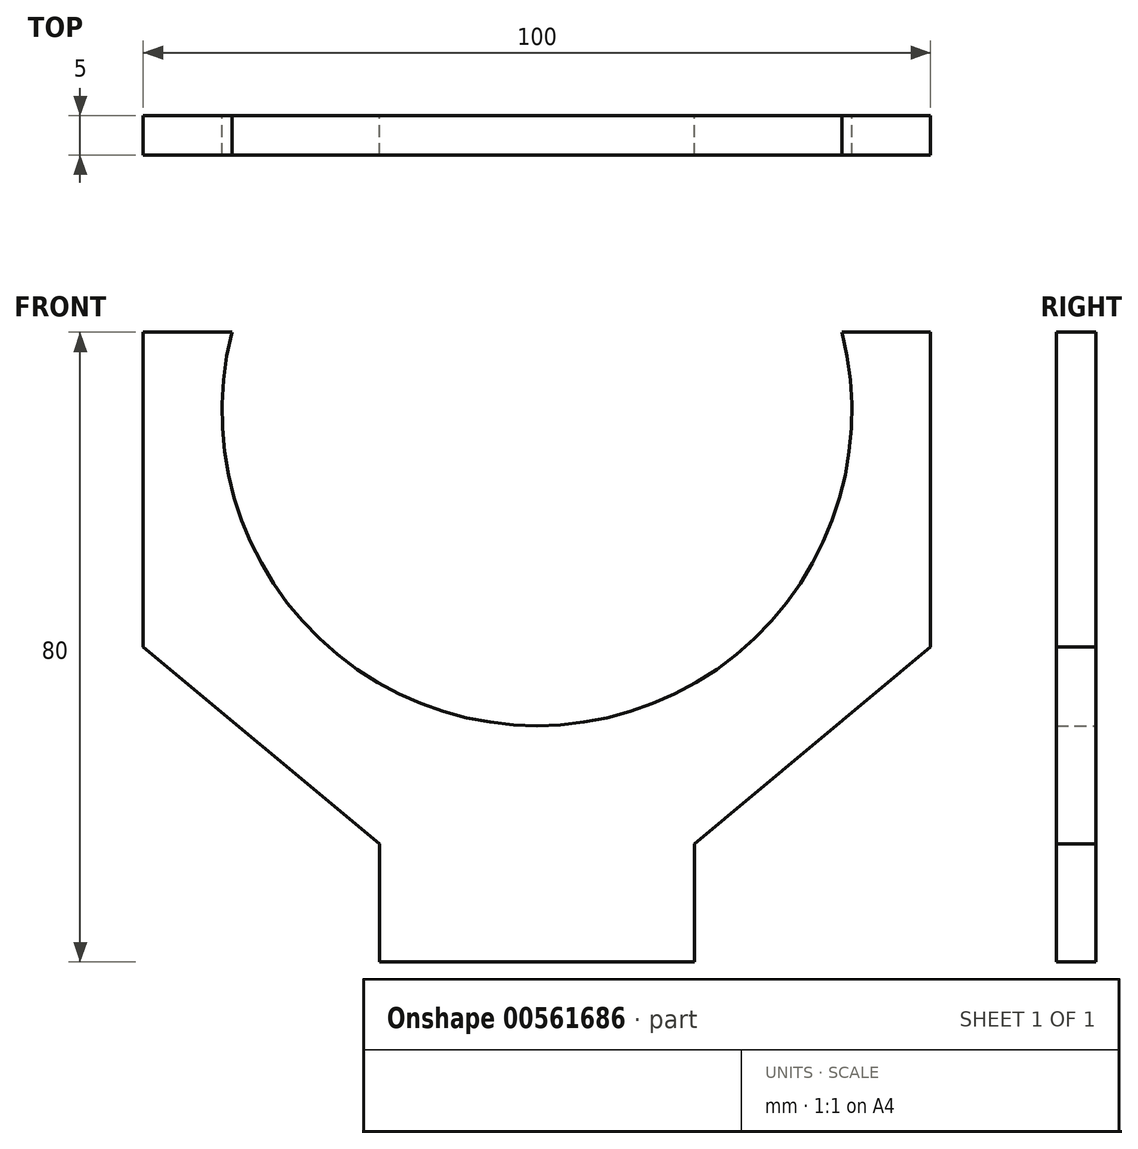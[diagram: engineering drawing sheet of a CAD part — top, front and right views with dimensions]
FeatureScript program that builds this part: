
annotation { "Feature Type Name" : "Feature", "Feature Type Description" : "" }
export const myFeature = defineFeature(function(context is Context, id is Id, definition is map)
    precondition{}
    {
        {
            var Q0;
            Q0=qCreatedBy(makeId("Front.planeOp"),FACE);
            var sketch = newSketch(context, id + "F0", { "sketchPlane" : qUnion([Q0])});
            skArc(sketch, "E0", {"start": v(-38.73, 80) * mm, "mid": v(0, 30) * mm, "end": v(38.73, 80) * mm});
            skLineSegment(sketch, "E1", {"start": v(0, 0) * mm, "end": v(20, 0) * mm});
            skLineSegment(sketch, "E2", {"start": v(20, 0) * mm, "end": v(20, 15) * mm});
            skLineSegment(sketch, "E3", {"start": v(20, 15) * mm, "end": v(50, 40) * mm});
            skLineSegment(sketch, "E4", {"start": v(50, 40) * mm, "end": v(50, 80) * mm});
            skLineSegment(sketch, "E5", {"start": v(50, 80) * mm, "end": v(38.73, 80) * mm});
            skLineSegment(sketch, "E6", {"start": v(0, 0) * mm, "end": v(-20, 0) * mm});
            skLineSegment(sketch, "E7", {"start": v(-20, 0) * mm, "end": v(-20, 15) * mm});
            skLineSegment(sketch, "E8", {"start": v(-20, 15) * mm, "end": v(-50, 40) * mm});
            skLineSegment(sketch, "E9", {"start": v(-50, 40) * mm, "end": v(-50, 80) * mm});
            skLineSegment(sketch, "E10", {"start": v(-50, 80) * mm, "end": v(-38.73, 80) * mm});
            skSolve(sketch);
        }
        {
            var Q0;
            Q0 = qSketchRegion(id + "F0", true);
            extrude(context, id + "F1", {"entities" : qUnion([Q0]), "depth" : 5 * mm, "offsetDistance" : 25 * mm});
        }
    });
